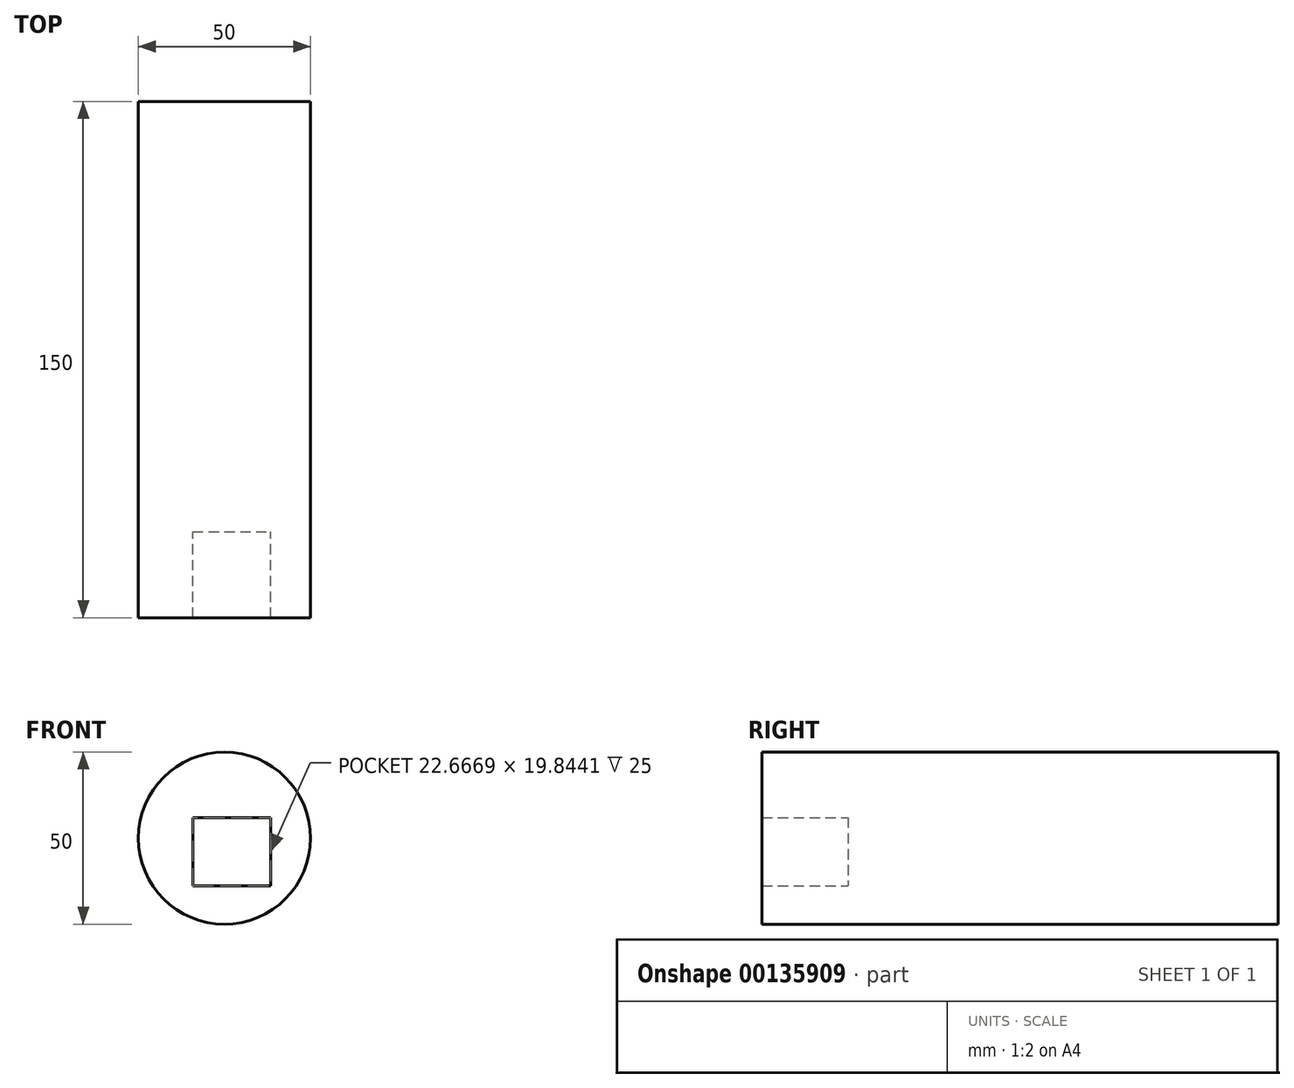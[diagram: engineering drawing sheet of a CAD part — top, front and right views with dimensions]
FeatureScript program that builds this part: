
annotation { "Feature Type Name" : "Feature", "Feature Type Description" : "" }
export const myFeature = defineFeature(function(context is Context, id is Id, definition is map)
    precondition{}
    {
        {
            var Q0;
            Q0=qCreatedBy(makeId("Front.planeOp"),FACE);
            var sketch = newSketch(context, id + "F0", { "sketchPlane" : qUnion([Q0])});
            skCircle(sketch, "E0", {"center": v(0, 0) * mm, "radius": 25 * mm});
            skSolve(sketch);
        }
        {
            var Q0;
            Q0=makeQuery(id+"F0.imprint","IMPRINT",FACE,{"disambiguationData":[TD([[makeQuery(id+"F0.imprint","IMPRINT",EDGE,{"derivedFrom":sQuery(id+"F0.wireOp",EDGE,"E0")}),1.0]])]});
            extrude(context, id + "F1", {"entities" : qUnion([Q0]), "depth" : 100 * mm});
        }
        {
            var Q0;
            Q0=makeQuery(id+"F1.opExtrude","CAP_FACE",FACE,{"disambiguationData":[OSD([sQuery(id+"F0.wireOp",EDGE,"E0")])],"isStart":false});
            extrude(context, id + "F2", {"entities" : qUnion([Q0]), "operationType" : NewBodyOperationType.ADD, "depth" : 25 * mm});
        }
        {
            var Q0;
            Q0=makeQuery(id+"F2.opExtrude","CAP_FACE",FACE,{"disambiguationData":[OSD([sQuery(id+"F0.wireOp",EDGE,"E0")])],"isStart":false});
            var sketch = newSketch(context, id + "F3", { "sketchPlane" : qUnion([Q0])});
            skLineSegment(sketch, "E1.bottom", {"start": v(-9.2, 6) * mm, "end": v(13.47, 6) * mm});
            skLineSegment(sketch, "E1.top", {"start": v(-9.2, -13.85) * mm, "end": v(13.47, -13.85) * mm});
            skLineSegment(sketch, "E1.left", {"start": v(-9.2, 6) * mm, "end": v(-9.2, -13.85) * mm});
            skLineSegment(sketch, "E1.right", {"start": v(13.47, 6) * mm, "end": v(13.47, -13.85) * mm});
            skSolve(sketch);
        }
        {
            var Q0;
            Q0=makeQuery(id+"F3.imprint","IMPRINT",FACE,{"disambiguationData":[TD([[makeQuery(id+"F3.imprint","IMPRINT",EDGE,{"derivedFrom":sQuery(id+"F3.wireOp",EDGE,"E1.bottom")}),1.0]])]});
            extrude(context, id + "F4", {"entities" : qUnion([Q0]), "operationType" : NewBodyOperationType.ADD, "depth" : 25 * mm});
        }
    });
